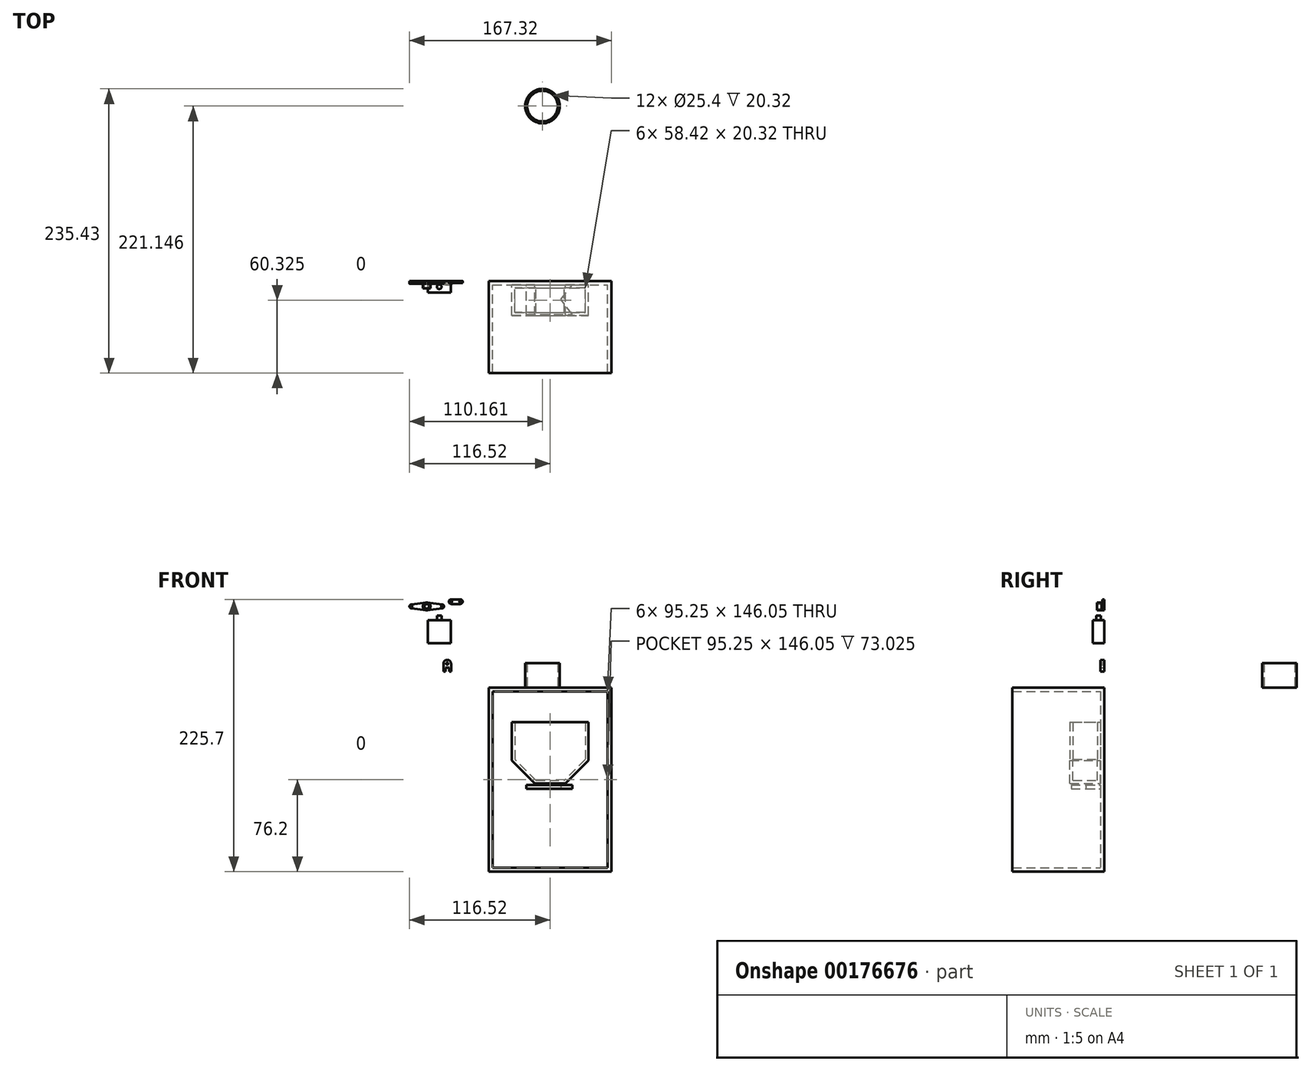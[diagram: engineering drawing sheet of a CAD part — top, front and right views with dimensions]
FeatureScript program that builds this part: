
annotation { "Feature Type Name" : "Feature", "Feature Type Description" : "" }
export const myFeature = defineFeature(function(context is Context, id is Id, definition is map)
    precondition{}
    {
        {
            var Q0;
            Q0=qCreatedBy(makeId("Front.planeOp"),FACE);
            var sketch = newSketch(context, id + "F0", { "sketchPlane" : qUnion([Q0])});
            skLineSegment(sketch, "E0.bottom", {"start": v(0, 0) * mm, "end": v(101.6, 0) * mm});
            skLineSegment(sketch, "E0.top", {"start": v(0, -152.4) * mm, "end": v(101.6, -152.4) * mm});
            skLineSegment(sketch, "E0.left", {"start": v(0, 0) * mm, "end": v(0, -152.4) * mm});
            skLineSegment(sketch, "E0.right", {"start": v(101.6, 0) * mm, "end": v(101.6, -152.4) * mm});
            skSolve(sketch);
        }
        {
            var Q0;
            Q0 = qSketchRegion(id + "F0", true);
            extrude(context, id + "F1", {"entities" : qUnion([Q0]), "depth" : 76.2 * mm});
        }
        {
            var Q0;
            Q0=makeQuery(id+"F1.opExtrude","CAP_FACE",FACE,{"disambiguationData":[OSD([sQuery(id+"F0.wireOp",EDGE,"E0.bottom"),sQuery(id+"F0.wireOp",EDGE,"E0.top"),sQuery(id+"F0.wireOp",EDGE,"E0.left"),sQuery(id+"F0.wireOp",EDGE,"E0.right")])],"isStart":false});
            shell(context, id + "F2", {"entities" : qUnion([Q0]), "thickness" : 3.17 * mm});
        }
        {
            var Q0;
            Q0=makeQuery(id+"F2.opShell","OFFSET_FACE",FACE,{"disambiguationData":[OSD([sQuery(id+"F0.wireOp",EDGE,"E0.bottom"),sQuery(id+"F0.wireOp",EDGE,"E0.top"),sQuery(id+"F0.wireOp",EDGE,"E0.left"),sQuery(id+"F0.wireOp",EDGE,"E0.right")])]});
            var sketch = newSketch(context, id + "F3", { "sketchPlane" : qUnion([Q0])});
            skLineSegment(sketch, "E1.bottom", {"start": v(19.05, -28.58) * mm, "end": v(82.55, -28.58) * mm});
            skLineSegment(sketch, "E1.top", {"start": v(38.1, -79.38) * mm, "end": v(63.5, -79.38) * mm});
            skLineSegment(sketch, "E1.left", {"start": v(19.05, -28.58) * mm, "end": v(19.05, -60.33) * mm});
            skLineSegment(sketch, "E1.right", {"start": v(82.55, -28.58) * mm, "end": v(82.55, -60.33) * mm});
            skLineSegment(sketch, "E2", {"start": v(82.55, -60.33) * mm, "end": v(63.5, -79.38) * mm});
            skLineSegment(sketch, "E3", {"start": v(63.5, -79.38) * mm, "end": v(38.1, -79.38) * mm});
            skLineSegment(sketch, "E4", {"start": v(38.1, -79.38) * mm, "end": v(19.05, -60.32) * mm});
            skLineSegment(sketch, "E5", {"start": v(19.05, -28.58) * mm, "end": v(3.18, -28.58) * mm, "construction": true});
            skLineSegment(sketch, "E6", {"start": v(82.55, -28.58) * mm, "end": v(98.43, -28.58) * mm, "construction": true});
            skSolve(sketch);
        }
        {
            var Q0;
            Q0 = qSketchRegion(id + "F3", true);
            extrude(context, id + "F4", {"entities" : qUnion([Q0]), "depth" : 25.4 * mm});
        }
        {
            var Q0;
            Q0=makeQuery(id+"F4.opExtrude","SWEPT_FACE",FACE,{"disambiguationData":[OSD([sQuery(id+"F3.wireOp",EDGE,"E1.bottom")])]});
            var Q1;
            Q1=makeQuery(id+"F4.opExtrude","SWEPT_FACE",FACE,{"disambiguationData":[OSD([sQuery(id+"F3.wireOp",EDGE,"E3")])]});
            shell(context, id + "F5", {"entities" : qUnion([Q0, Q1]), "thickness" : 2.54 * mm});
        }
        {
            var Q0;
            Q0=makeQuery(id+"F2.opShell","OFFSET_FACE",FACE,{"disambiguationData":[OSD([sQuery(id+"F0.wireOp",EDGE,"E0.bottom"),sQuery(id+"F0.wireOp",EDGE,"E0.top"),sQuery(id+"F0.wireOp",EDGE,"E0.left"),sQuery(id+"F0.wireOp",EDGE,"E0.right")])]});
            var sketch = newSketch(context, id + "F6", { "sketchPlane" : qUnion([Q0])});
            skLineSegment(sketch, "E7.bottom", {"start": v(31.06, -80.47) * mm, "end": v(69.16, -80.47) * mm});
            skLineSegment(sketch, "E7.top", {"start": v(31.06, -83.64) * mm, "end": v(69.16, -83.64) * mm});
            skLineSegment(sketch, "E7.left", {"start": v(31.06, -80.47) * mm, "end": v(31.06, -83.64) * mm});
            skLineSegment(sketch, "E7.right", {"start": v(69.16, -80.47) * mm, "end": v(69.16, -83.64) * mm});
            skSolve(sketch);
        }
        {
            var Q0;
            Q0 = qSketchRegion(id + "F6", true);
            extrude(context, id + "F7", {"entities" : qUnion([Q0]), "depth" : 24.38 * mm});
        }
        {
            var Q0;
            Q0=makeQuery(id+"F7.opExtrude","SWEPT_FACE",FACE,{"disambiguationData":[OSD([sQuery(id+"F6.wireOp",EDGE,"E7.top")])]});
            var sketch = newSketch(context, id + "F8", { "sketchPlane" : qUnion([Q0])});
            skLineSegment(sketch, "E8", {"start": v(69.16, 27.56) * mm, "end": v(59.63, 15.37) * mm});
            skLineSegment(sketch, "E9", {"start": v(59.63, 15.37) * mm, "end": v(69.16, 3.17) * mm});
            skLineSegment(sketch, "E10", {"start": v(69.16, 27.56) * mm, "end": v(69.16, 3.17) * mm});
            skSolve(sketch);
        }
        {
            var Q0;
            Q0 = qSketchRegion(id + "F8", true);
            extrude(context, id + "F9", {"entities" : qUnion([Q0]), "operationType" : NewBodyOperationType.REMOVE, "endBound" : BoundingType.UP_TO_NEXT, "oppositeDirection" : true, "depth" : 25.4 * mm});
        }
        {
            var Q0;
            Q0=qCreatedBy(makeId("Top.planeOp"),FACE);
            var sketch = newSketch(context, id + "F10", { "sketchPlane" : qUnion([Q0])});
            skCircle(sketch, "E11", {"center": v(44.44, 144.95) * mm, "radius": 14.29 * mm});
            skCircle(sketch, "E12", {"center": v(44.44, 144.95) * mm, "radius": 12.7 * mm});
            skSolve(sketch);
        }
        {
            var Q0;
            Q0 = qSketchRegion(id + "F10", true);
            extrude(context, id + "F11", {"entities" : qUnion([Q0]), "depth" : 20.32 * mm});
        }
        {
            var Q0;
            Q0=qCreatedBy(makeId("Front.planeOp"),FACE);
            var sketch = newSketch(context, id + "F12", { "sketchPlane" : qUnion([Q0])});
            skLineSegment(sketch, "E13", {"start": v(-37.61, 13.58) * mm, "end": v(-37.61, 19.93) * mm});
            skArc(sketch, "E14", {"start": v(-31.26, 19.93) * mm, "mid": v(-34.44, 23.1) * mm, "end": v(-37.61, 19.93) * mm});
            skLineSegment(sketch, "E15", {"start": v(-31.26, 19.93) * mm, "end": v(-31.26, 13.58) * mm});
            skLineSegment(sketch, "E16", {"start": v(-31.26, 13.58) * mm, "end": v(-32.85, 13.58) * mm});
            skLineSegment(sketch, "E17.top", {"start": v(-36.02, 16.76) * mm, "end": v(-32.85, 16.76) * mm});
            skLineSegment(sketch, "E17.left", {"start": v(-36.02, 13.58) * mm, "end": v(-36.02, 16.76) * mm});
            skLineSegment(sketch, "E17.right", {"start": v(-32.85, 13.58) * mm, "end": v(-32.85, 16.76) * mm});
            skLineSegment(sketch, "E18.trimOffspring", {"start": v(-36.02, 13.58) * mm, "end": v(-37.61, 13.58) * mm});
            skCircle(sketch, "E19", {"center": v(-34.44, 19.93) * mm, "radius": 0.8 * mm});
            skSolve(sketch);
        }
        {
            var Q0;
            Q0 = qSketchRegion(id + "F12", true);
            extrude(context, id + "F13", {"entities" : qUnion([Q0]), "depth" : 3.17 * mm});
        }
        {
            var Q0;
            Q0=qCreatedBy(makeId("Front.planeOp"),FACE);
            var sketch = newSketch(context, id + "F14", { "sketchPlane" : qUnion([Q0])});
            skLineSegment(sketch, "E20.bottom", {"start": v(-50.62, 56) * mm, "end": v(-31.57, 56) * mm});
            skLineSegment(sketch, "E20.top", {"start": v(-50.62, 36.94) * mm, "end": v(-31.57, 36.94) * mm});
            skLineSegment(sketch, "E20.left", {"start": v(-50.62, 56) * mm, "end": v(-50.62, 36.94) * mm});
            skLineSegment(sketch, "E20.right", {"start": v(-31.57, 56) * mm, "end": v(-31.57, 36.94) * mm});
            skSolve(sketch);
        }
        {
            var Q0;
            Q0 = qSketchRegion(id + "F14", true);
            extrude(context, id + "F15", {"entities" : qUnion([Q0]), "depth" : 9.52 * mm});
        }
        {
            var Q0;
            Q0=makeQuery(id+"F15.opExtrude","SWEPT_FACE",FACE,{"disambiguationData":[OSD([sQuery(id+"F14.wireOp",EDGE,"E20.bottom")])]});
            var sketch = newSketch(context, id + "F16", { "sketchPlane" : qUnion([Q0])});
            skCircle(sketch, "E21", {"center": v(-41.1, -4.76) * mm, "radius": 1.9 * mm});
            skPoint(sketch, "E21.centerSnap0", {"position": v(-50.62, -4.76) * mm});
            skLineSegment(sketch, "E22", {"start": v(-50.62, 0) * mm, "end": v(-31.57, -9.52) * mm, "construction": true});
            skSolve(sketch);
        }
        {
            var Q0;
            Q0 = qSketchRegion(id + "F16", true);
            extrude(context, id + "F17", {"entities" : qUnion([Q0]), "operationType" : NewBodyOperationType.ADD, "depth" : 3.8 * mm});
        }
        {
            var Q0;
            Q0=qCreatedBy(makeId("Front.planeOp"),FACE);
            var sketch = newSketch(context, id + "F18", { "sketchPlane" : qUnion([Q0])});
            skCircle(sketch, "E23", {"center": v(-51.43, 67.45) * mm, "radius": 3.18 * mm});
            skCircle(sketch, "E24", {"center": v(-38.73, 67.45) * mm, "radius": 1.59 * mm});
            skCircle(sketch, "E25", {"center": v(-64.13, 67.45) * mm, "radius": 1.59 * mm});
            skLineSegment(sketch, "E26", {"start": v(-64.13, 67.45) * mm, "end": v(-38.73, 67.45) * mm, "construction": true});
            skLineSegment(sketch, "E27", {"start": v(-64.33, 69.02) * mm, "end": v(-51.83, 70.6) * mm});
            skLineSegment(sketch, "E28", {"start": v(-38.53, 65.87) * mm, "end": v(-51.04, 64.3) * mm});
            skLineSegment(sketch, "E29", {"start": v(-51.83, 64.3) * mm, "end": v(-64.33, 65.87) * mm});
            skLineSegment(sketch, "E30", {"start": v(-51.04, 70.6) * mm, "end": v(-38.53, 69.02) * mm});
            skSolve(sketch);
        }
        {
            var Q0;
            Q0 = qSketchRegion(id + "F18", true);
            extrude(context, id + "F19", {"entities" : qUnion([Q0]), "depth" : 2.3 * mm});
        }
        {
            var Q0;
            Q0=sQuery(id+"F18.wireOp",VERTEX,"E26.start");
            var Q1;
            Q1=sQuery(id+"F18.wireOp",VERTEX,"E24.center");
            var Q2;
            Q2=makeQuery(id+"F19.opExtrude","SWEPT_BODY",BODY,{"disambiguationData":[OSD([sQuery(id+"F18.wireOp",EDGE,"E23"),sQuery(id+"F18.wireOp",EDGE,"E24"),sQuery(id+"F18.wireOp",EDGE,"E25"),sQuery(id+"F18.wireOp",EDGE,"E27"),sQuery(id+"F18.wireOp",EDGE,"E28"),sQuery(id+"F18.wireOp",EDGE,"E29"),sQuery(id+"F18.wireOp",EDGE,"E30")])]});
            hole(context, id + "F20", {"style" : HoleStyle.SIMPLE, "endStyle" : HoleEndStyle.THROUGH, "oppositeDirection" : true, "holeDiameter" : 1.52 * mm, "locations" : qUnion([Q0, Q1]), "scope" : qUnion([Q2]), "isTappedThrough" : true});
        }
        {
            var Q0;
            Q0=makeQuery(id+"F19.opExtrude","CAP_FACE",FACE,{"disambiguationData":[OSD([sQuery(id+"F18.wireOp",EDGE,"E23"),sQuery(id+"F18.wireOp",EDGE,"E24"),sQuery(id+"F18.wireOp",EDGE,"E25"),sQuery(id+"F18.wireOp",EDGE,"E27"),sQuery(id+"F18.wireOp",EDGE,"E28"),sQuery(id+"F18.wireOp",EDGE,"E29"),sQuery(id+"F18.wireOp",EDGE,"E30")])],"isStart":false});
            var sketch = newSketch(context, id + "F21", { "sketchPlane" : qUnion([Q0])});
            skCircle(sketch, "E31", {"center": v(-51.43, 67.45) * mm, "radius": 3.18 * mm});
            skCircle(sketch, "E32", {"center": v(-51.43, 67.45) * mm, "radius": 1.9 * mm});
            skSolve(sketch);
        }
        {
            var Q0;
            Q0 = qSketchRegion(id + "F21", true);
            extrude(context, id + "F22", {"entities" : qUnion([Q0]), "operationType" : NewBodyOperationType.ADD, "depth" : 3.8 * mm});
        }
        {
            var Q0;
            Q0=qCreatedBy(makeId("Front.planeOp"),FACE);
            var sketch = newSketch(context, id + "F23", { "sketchPlane" : qUnion([Q0])});
            skCircle(sketch, "E33", {"center": v(-31.21, 71.4) * mm, "radius": 1.9 * mm});
            skCircle(sketch, "E34", {"center": v(-23.6, 71.4) * mm, "radius": 1.9 * mm});
            skLineSegment(sketch, "E35", {"start": v(-31.21, 73.3) * mm, "end": v(-23.6, 73.3) * mm});
            skLineSegment(sketch, "E36", {"start": v(-31.21, 69.5) * mm, "end": v(-23.6, 69.5) * mm});
            skCircle(sketch, "E37", {"center": v(-31.21, 71.4) * mm, "radius": 0.8 * mm});
            skCircle(sketch, "E38", {"center": v(-23.6, 71.4) * mm, "radius": 0.8 * mm});
            skSolve(sketch);
        }
        {
            var Q0;
            Q0 = qSketchRegion(id + "F23", true);
            extrude(context, id + "F24", {"entities" : qUnion([Q0]), "depth" : 1.59 * mm});
        }
    });
